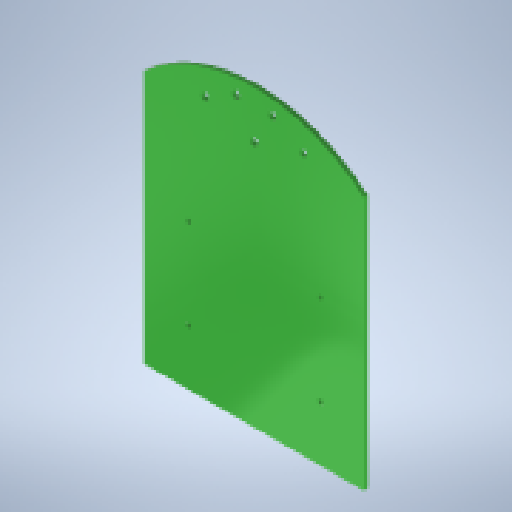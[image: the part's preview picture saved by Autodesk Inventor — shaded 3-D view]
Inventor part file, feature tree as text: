
AUTODESK INVENTOR PART (.ipt)
format: ipt  version: 2025.3 (Build 293356000, 356)  size: 158,208 bytes
history: native  units: mm
features: sketch x4, hole x3, other x1, extrude x1
ambient origin geometry x8: Origin, YZ Plane, XZ Plane, XY Plane, X Axis, Y Axis, Z Axis, Center Point
bodies: Body1 (feature_tree)
feature tree (9):
  other  "ソリッド1"
  extrude  "基板"  Depth=130.0mm
  hole  "モータ取付穴"  [1 undecoded]
  hole  "ボールキャスター取付穴"  [1 undecoded]
  hole  "穴4"  [1 undecoded]
  sketch  "スケッチ1"
  sketch  "スケッチ2"
  sketch  "スケッチ3"
  sketch  "スケッチ5"
note: 3 required parameter values undecoded (feature->parameter linkage not recoverable at this tier; creation-order binding heuristic only, values carry confidence <= 0.55)
